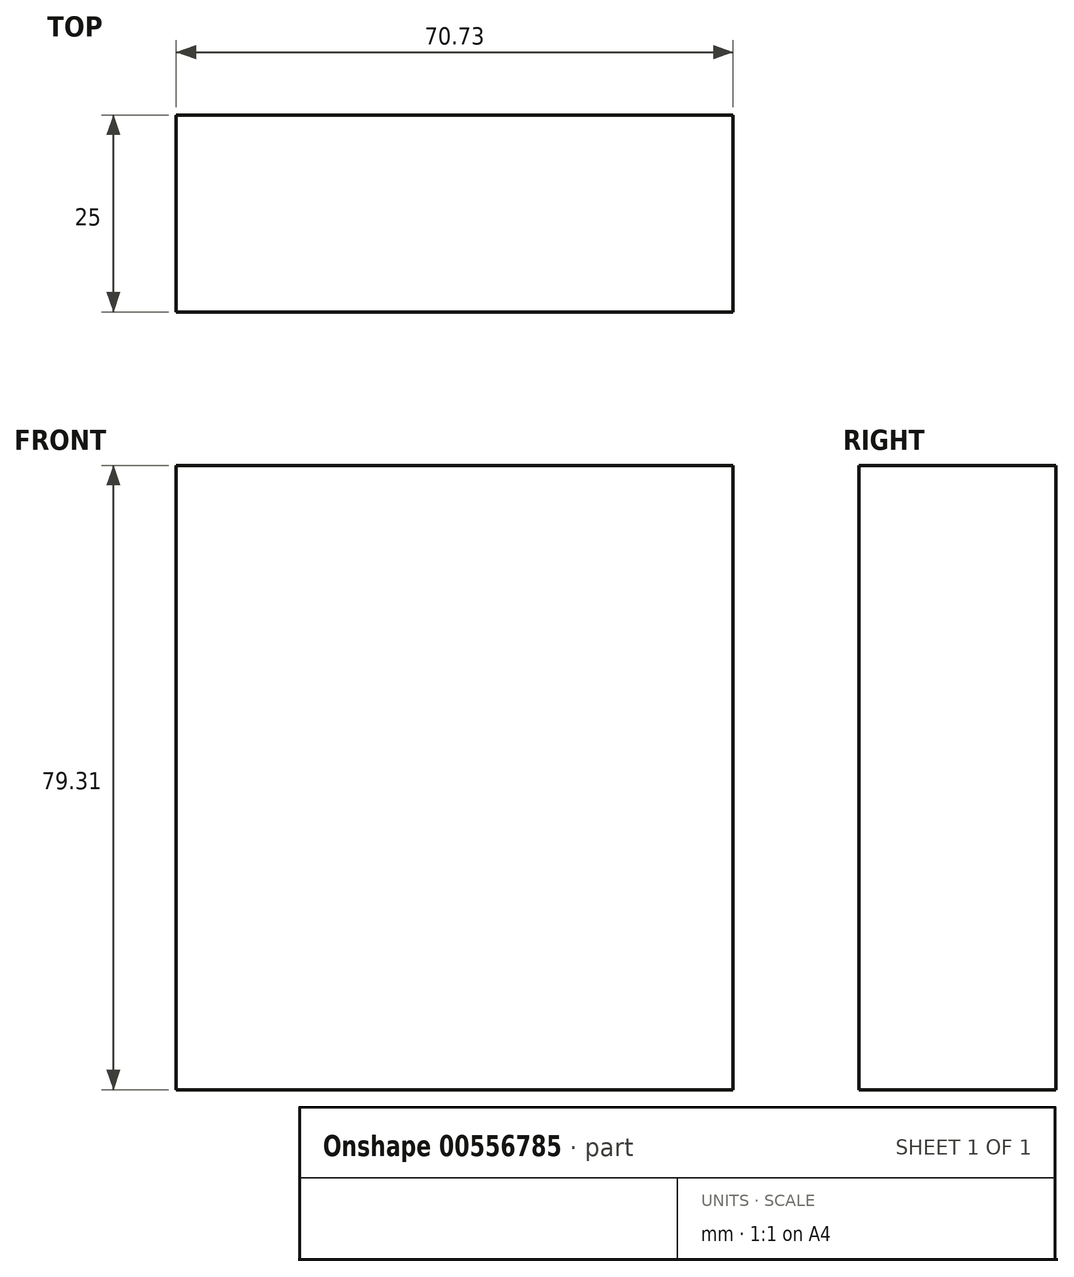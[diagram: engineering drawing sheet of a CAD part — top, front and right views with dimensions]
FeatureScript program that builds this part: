
annotation { "Feature Type Name" : "Feature", "Feature Type Description" : "" }
export const myFeature = defineFeature(function(context is Context, id is Id, definition is map)
    precondition{}
    {
        {
            var Q0;
            Q0=qCreatedBy(makeId("Front.planeOp"),FACE);
            var sketch = newSketch(context, id + "F0", { "sketchPlane" : qUnion([Q0])});
            skLineSegment(sketch, "E0.bottom", {"start": v(-50.7, 54.21) * mm, "end": v(20.04, 54.21) * mm});
            skLineSegment(sketch, "E0.top", {"start": v(-50.7, -25.1) * mm, "end": v(20.04, -25.1) * mm});
            skLineSegment(sketch, "E0.left", {"start": v(-50.7, 54.21) * mm, "end": v(-50.7, -25.1) * mm});
            skLineSegment(sketch, "E0.right", {"start": v(20.04, 54.21) * mm, "end": v(20.04, -25.1) * mm});
            skSolve(sketch);
        }
        {
            var Q0;
            Q0=makeQuery(id+"F0.imprint","IMPRINT",FACE,{"disambiguationData":[TD([[makeQuery(id+"F0.imprint","IMPRINT",EDGE,{"derivedFrom":sQuery(id+"F0.wireOp",EDGE,"E0.bottom")}),-1.0]])]});
            extrude(context, id + "F1", {"entities" : qUnion([Q0]), "depth" : 25 * mm, "offsetDistance" : 25 * mm});
        }
    });
